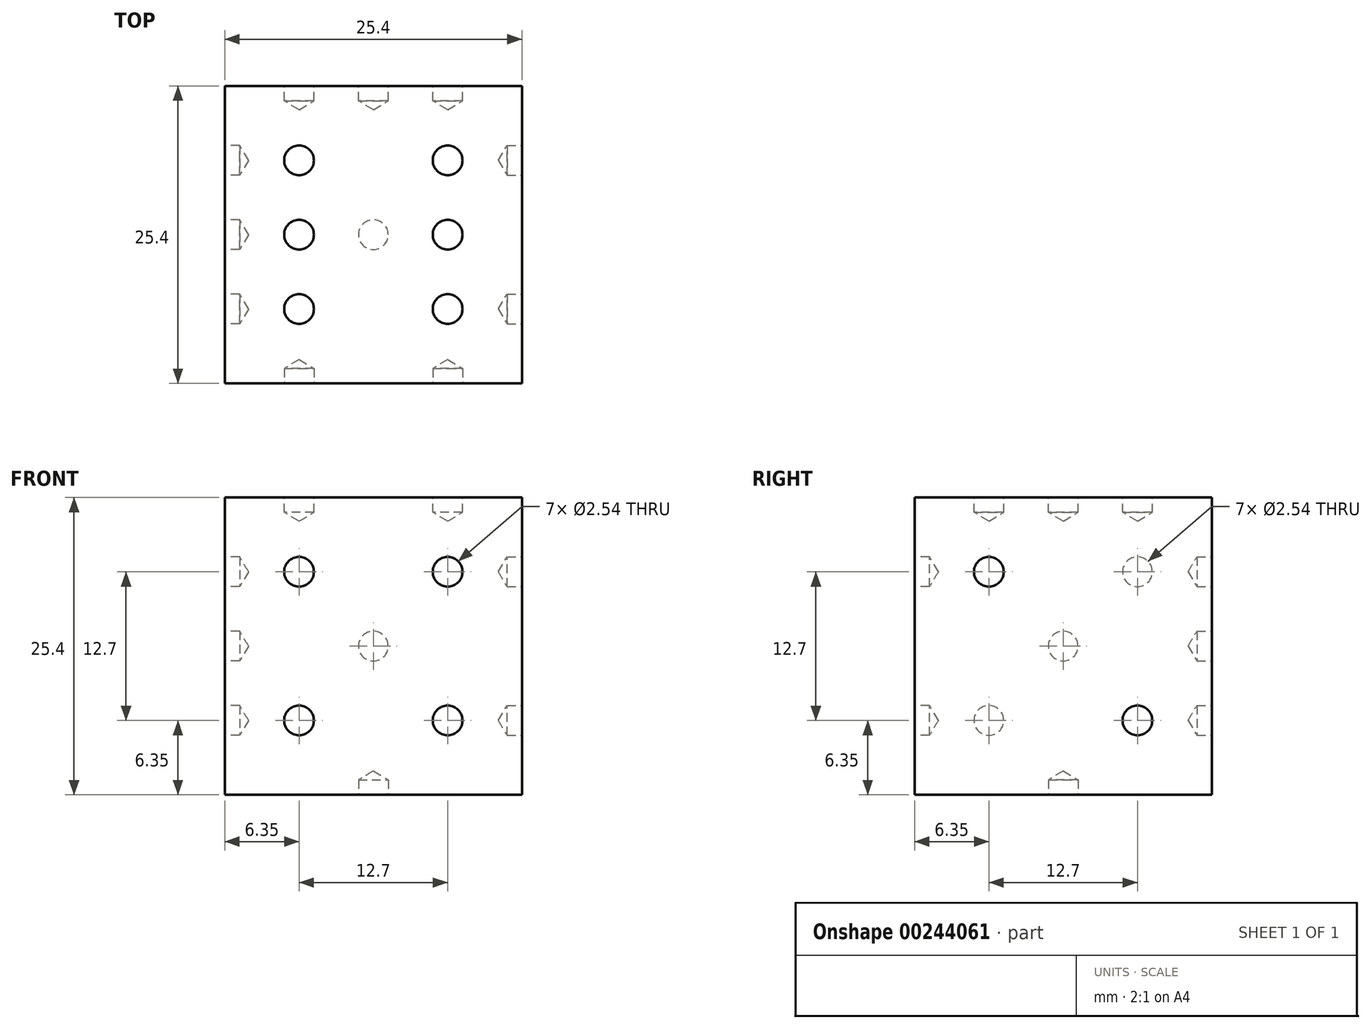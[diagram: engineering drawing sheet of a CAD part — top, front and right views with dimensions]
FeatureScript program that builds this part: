
annotation { "Feature Type Name" : "Feature", "Feature Type Description" : "" }
export const myFeature = defineFeature(function(context is Context, id is Id, definition is map)
    precondition{}
    {
        {
            var Q0;
            Q0=qCreatedBy(makeId("Top.planeOp"),FACE);
            var sketch = newSketch(context, id + "F0", { "sketchPlane" : qUnion([Q0])});
            skLineSegment(sketch, "E0.bottom", {"start": v(12.7, -12.7) * mm, "end": v(-12.7, -12.7) * mm});
            skLineSegment(sketch, "E0.top", {"start": v(12.7, 12.7) * mm, "end": v(-12.7, 12.7) * mm});
            skLineSegment(sketch, "E0.left", {"start": v(12.7, -12.7) * mm, "end": v(12.7, 12.7) * mm});
            skLineSegment(sketch, "E0.right", {"start": v(-12.7, -12.7) * mm, "end": v(-12.7, 12.7) * mm});
            skPoint(sketch, "E0.middle", {"position": v(0, 0) * mm});
            skSolve(sketch);
        }
        {
            var Q0;
            Q0=makeQuery(id+"F0.imprint","IMPRINT",FACE,{"disambiguationData":[TD([[makeQuery(id+"F0.imprint","IMPRINT",EDGE,{"derivedFrom":sQuery(id+"F0.wireOp",EDGE,"E0.bottom")}),-1.0]])]});
            extrude(context, id + "F1", {"entities" : qUnion([Q0]), "depth" : 25.4 * mm});
        }
        {
            var Q0;
            Q0=makeQuery(id+"F1.opExtrude","SWEPT_FACE",FACE,{"disambiguationData":[OSD([sQuery(id+"F0.wireOp",EDGE,"E0.top")])]});
            var sketch = newSketch(context, id + "F2", { "sketchPlane" : qUnion([Q0])});
            skPoint(sketch, "E1", {"position": v(0, 12.7) * mm});
            skPoint(sketch, "E2.orphan", {"position": v(12.7, 0) * mm});
            skPoint(sketch, "E3", {"position": v(-6.35, 19.05) * mm});
            skPoint(sketch, "E4.start.orphan", {"position": v(-12.7, 25.4) * mm});
            skPoint(sketch, "E5", {"position": v(6.35, 6.35) * mm});
            skSolve(sketch);
        }
        {
            var Q0;
            Q0=makeQuery(id+"F1.opExtrude","SWEPT_FACE",FACE,{"disambiguationData":[OSD([sQuery(id+"F0.wireOp",EDGE,"E0.left")])]});
            var sketch = newSketch(context, id + "F3", { "sketchPlane" : qUnion([Q0])});
            skPoint(sketch, "E6.endSnap0", {"position": v(12.7, 12.7) * mm});
            skPoint(sketch, "E6.endSnap1", {"position": v(0, 25.4) * mm});
            skPoint(sketch, "E7", {"position": v(0, 12.7) * mm});
            skPoint(sketch, "E8", {"position": v(-6.35, 19.05) * mm});
            skPoint(sketch, "E9", {"position": v(6.35, 6.35) * mm});
            skPoint(sketch, "E10.orphan", {"position": v(-12.7, 25.4) * mm});
            skPoint(sketch, "E11.end.orphan", {"position": v(12.7, 0) * mm});
            skSolve(sketch);
        }
        {
            var Q0;
            Q0=makeQuery(id+"F1.opExtrude","SWEPT_FACE",FACE,{"disambiguationData":[OSD([sQuery(id+"F0.wireOp",EDGE,"E0.right")])]});
            var sketch = newSketch(context, id + "F4", { "sketchPlane" : qUnion([Q0])});
            skPoint(sketch, "E12.endSnap0", {"position": v(12.7, 12.7) * mm});
            skPoint(sketch, "E13", {"position": v(-6.35, 6.35) * mm});
            skPoint(sketch, "E14", {"position": v(0, 12.7) * mm});
            skPoint(sketch, "E15.1.0", {"position": v(6.35, 6.35) * mm});
            skPoint(sketch, "E15.2.0", {"position": v(6.35, 19.05) * mm});
            skPoint(sketch, "E15.3.0", {"position": v(-6.35, 19.05) * mm});
            skPoint(sketch, "E16.orphan", {"position": v(-12.7, 0) * mm});
            skSolve(sketch);
        }
        {
            var Q0;
            Q0=makeQuery(id+"F1.opExtrude","SWEPT_FACE",FACE,{"disambiguationData":[OSD([sQuery(id+"F0.wireOp",EDGE,"E0.bottom")])]});
            var sketch = newSketch(context, id + "F5", { "sketchPlane" : qUnion([Q0])});
            skPoint(sketch, "E17.endSnap0", {"position": v(12.7, 12.7) * mm});
            skPoint(sketch, "E18", {"position": v(-6.35, 6.35) * mm});
            skPoint(sketch, "E19.1.0", {"position": v(6.35, 6.35) * mm});
            skPoint(sketch, "E19.2.0", {"position": v(6.35, 19.05) * mm});
            skPoint(sketch, "E19.3.0", {"position": v(-6.35, 19.05) * mm});
            skPoint(sketch, "E19.center", {"position": v(0, 12.7) * mm});
            skPoint(sketch, "E17.start.orphan", {"position": v(-12.7, 0) * mm});
            skSolve(sketch);
        }
        {
            var Q0;
            Q0=makeQuery(id+"F1.opExtrude","CAP_FACE",FACE,{"disambiguationData":[OSD([sQuery(id+"F0.wireOp",EDGE,"E0.bottom"),sQuery(id+"F0.wireOp",EDGE,"E0.top"),sQuery(id+"F0.wireOp",EDGE,"E0.left"),sQuery(id+"F0.wireOp",EDGE,"E0.right")])],"isStart":false});
            var sketch = newSketch(context, id + "F6", { "sketchPlane" : qUnion([Q0])});
            skLineSegment(sketch, "E20", {"start": v(-12.7, 12.7) * mm, "end": v(-12.7, 6.35) * mm});
            skLineSegment(sketch, "E21", {"start": v(-12.7, 6.35) * mm, "end": v(-12.7, 0) * mm});
            skLineSegment(sketch, "E22", {"start": v(-12.7, 0) * mm, "end": v(-12.7, -6.35) * mm});
            skLineSegment(sketch, "E23", {"start": v(-12.7, -6.35) * mm, "end": v(-12.7, -12.7) * mm});
            skLineSegment(sketch, "E24", {"start": v(-6.35, 6.35) * mm, "end": v(-6.35, -6.35) * mm});
            skPoint(sketch, "E25.orphan", {"position": v(0, 6.35) * mm});
            skPoint(sketch, "E26", {"position": v(-6.35, 0) * mm});
            skPoint(sketch, "E27", {"position": v(-6.35, 6.35) * mm});
            skPoint(sketch, "E28", {"position": v(-6.35, -6.35) * mm});
            skPoint(sketch, "E29.MirrorP", {"position": v(6.35, -6.35) * mm});
            skPoint(sketch, "E30.MirrorP", {"position": v(6.35, 0) * mm});
            skPoint(sketch, "E31.MirrorP", {"position": v(6.35, 6.35) * mm});
            skSolve(sketch);
        }
        {
            var Q0;
            Q0=sQuery(id+"F6.wireOp",VERTEX,"E27");
            var Q1;
            Q1=sQuery(id+"F6.wireOp",VERTEX,"E31.MirrorP");
            var Q2;
            Q2=sQuery(id+"F6.wireOp",VERTEX,"E26");
            var Q3;
            Q3=sQuery(id+"F6.wireOp",VERTEX,"E28");
            var Q4;
            Q4=sQuery(id+"F6.wireOp",VERTEX,"E30.MirrorP");
            var Q5;
            Q5=sQuery(id+"F6.wireOp",VERTEX,"E29.MirrorP");
            var Q6;
            Q6=makeQuery(id+"F1.opExtrude","SWEPT_BODY",BODY,{"disambiguationData":[OSD([sQuery(id+"F0.wireOp",EDGE,"E0.bottom"),sQuery(id+"F0.wireOp",EDGE,"E0.top"),sQuery(id+"F0.wireOp",EDGE,"E0.left"),sQuery(id+"F0.wireOp",EDGE,"E0.right")])]});
            hole(context, id + "F7", {"style" : HoleStyle.SIMPLE, "endStyle" : HoleEndStyle.BLIND, "holeDiameter" : 2.54 * mm, "holeDepth" : 1.27 * mm, "startFromSketch" : true, "locations" : qUnion([Q0, Q1, Q2, Q3, Q4, Q5]), "scope" : qUnion([Q6])});
        }
        {
            var Q0;
            Q0=sQuery(id+"F5.wireOp",VERTEX,"E19.3.0");
            var Q1;
            Q1=sQuery(id+"F5.wireOp",VERTEX,"E19.2.0");
            var Q2;
            Q2=sQuery(id+"F5.wireOp",VERTEX,"E19.1.0");
            var Q3;
            Q3=sQuery(id+"F5.wireOp",VERTEX,"E18");
            var Q4;
            Q4=makeQuery(id+"F1.opExtrude","SWEPT_BODY",BODY,{"disambiguationData":[OSD([sQuery(id+"F0.wireOp",EDGE,"E0.bottom"),sQuery(id+"F0.wireOp",EDGE,"E0.top"),sQuery(id+"F0.wireOp",EDGE,"E0.left"),sQuery(id+"F0.wireOp",EDGE,"E0.right")])]});
            hole(context, id + "F8", {"style" : HoleStyle.SIMPLE, "endStyle" : HoleEndStyle.BLIND, "holeDiameter" : 2.54 * mm, "holeDepth" : 1.27 * mm, "startFromSketch" : true, "locations" : qUnion([Q0, Q1, Q2, Q3]), "scope" : qUnion([Q4])});
        }
        {
            var Q0;
            Q0=sQuery(id+"F4.wireOp",VERTEX,"E13");
            var Q1;
            Q1=sQuery(id+"F4.wireOp",VERTEX,"E15.3.0");
            var Q2;
            Q2=sQuery(id+"F4.wireOp",VERTEX,"E15.2.0");
            var Q3;
            Q3=sQuery(id+"F4.wireOp",VERTEX,"E15.1.0");
            var Q4;
            Q4=sQuery(id+"F4.wireOp",VERTEX,"E14");
            var Q5;
            Q5=makeQuery(id+"F1.opExtrude","SWEPT_BODY",BODY,{"disambiguationData":[OSD([sQuery(id+"F0.wireOp",EDGE,"E0.bottom"),sQuery(id+"F0.wireOp",EDGE,"E0.top"),sQuery(id+"F0.wireOp",EDGE,"E0.left"),sQuery(id+"F0.wireOp",EDGE,"E0.right")])]});
            hole(context, id + "F9", {"style" : HoleStyle.SIMPLE, "endStyle" : HoleEndStyle.BLIND, "holeDiameter" : 2.54 * mm, "holeDepth" : 1.27 * mm, "startFromSketch" : true, "locations" : qUnion([Q0, Q1, Q2, Q3, Q4]), "scope" : qUnion([Q5])});
        }
        {
            var Q0;
            Q0=sQuery(id+"F2.wireOp",VERTEX,"E5");
            var Q1;
            Q1=sQuery(id+"F2.wireOp",VERTEX,"E1");
            var Q2;
            Q2=sQuery(id+"F2.wireOp",VERTEX,"E3");
            var Q3;
            Q3=makeQuery(id+"F1.opExtrude","SWEPT_BODY",BODY,{"disambiguationData":[OSD([sQuery(id+"F0.wireOp",EDGE,"E0.bottom"),sQuery(id+"F0.wireOp",EDGE,"E0.top"),sQuery(id+"F0.wireOp",EDGE,"E0.left"),sQuery(id+"F0.wireOp",EDGE,"E0.right")])]});
            hole(context, id + "F10", {"style" : HoleStyle.SIMPLE, "endStyle" : HoleEndStyle.BLIND, "holeDiameter" : 2.54 * mm, "holeDepth" : 1.27 * mm, "startFromSketch" : true, "locations" : qUnion([Q0, Q1, Q2]), "scope" : qUnion([Q3])});
        }
        {
            var Q0;
            Q0=sQuery(id+"F0.wireOp",VERTEX,"E0.middle");
            var Q1;
            Q1=makeQuery(id+"F1.opExtrude","SWEPT_BODY",BODY,{"disambiguationData":[OSD([sQuery(id+"F0.wireOp",EDGE,"E0.bottom"),sQuery(id+"F0.wireOp",EDGE,"E0.top"),sQuery(id+"F0.wireOp",EDGE,"E0.left"),sQuery(id+"F0.wireOp",EDGE,"E0.right")])]});
            hole(context, id + "F11", {"style" : HoleStyle.SIMPLE, "endStyle" : HoleEndStyle.BLIND, "oppositeDirection" : true, "holeDiameter" : 2.54 * mm, "holeDepth" : 1.27 * mm, "startFromSketch" : true, "locations" : qUnion([Q0]), "scope" : qUnion([Q1])});
        }
        {
            var Q0;
            Q0=sQuery(id+"F3.wireOp",VERTEX,"E8");
            var Q1;
            Q1=sQuery(id+"F3.wireOp",VERTEX,"E9");
            var Q2;
            Q2=makeQuery(id+"F1.opExtrude","SWEPT_BODY",BODY,{"disambiguationData":[OSD([sQuery(id+"F0.wireOp",EDGE,"E0.bottom"),sQuery(id+"F0.wireOp",EDGE,"E0.top"),sQuery(id+"F0.wireOp",EDGE,"E0.left"),sQuery(id+"F0.wireOp",EDGE,"E0.right")])]});
            hole(context, id + "F12", {"style" : HoleStyle.SIMPLE, "endStyle" : HoleEndStyle.BLIND, "holeDiameter" : 2.54 * mm, "holeDepth" : 1.27 * mm, "startFromSketch" : true, "locations" : qUnion([Q0, Q1]), "scope" : qUnion([Q2])});
        }
    });
